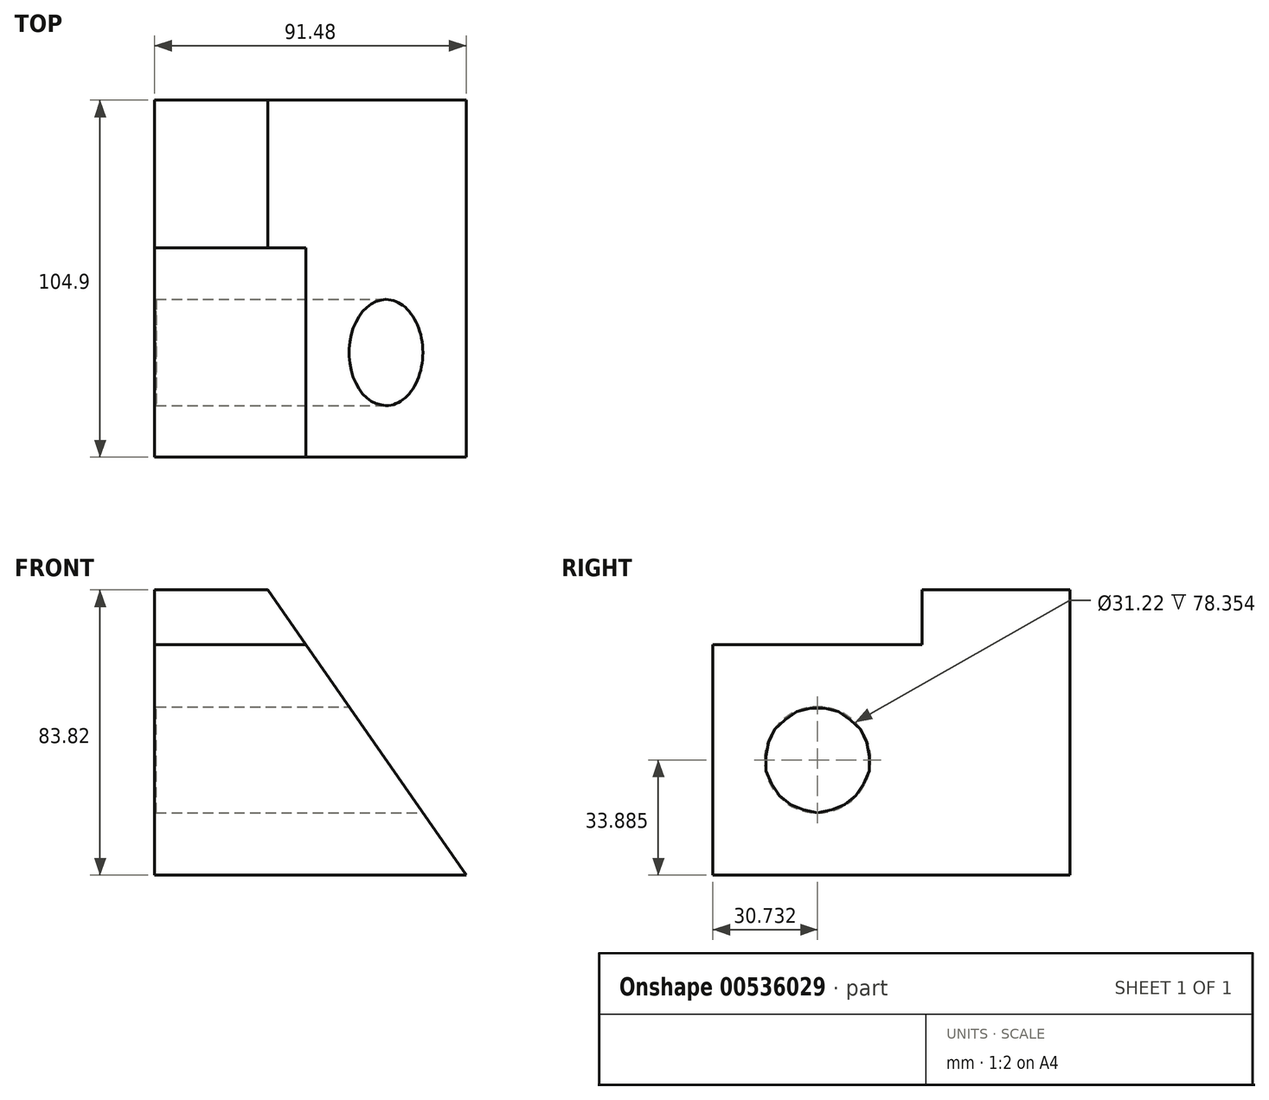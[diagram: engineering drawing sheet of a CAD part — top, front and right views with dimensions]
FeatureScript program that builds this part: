
annotation { "Feature Type Name" : "Feature", "Feature Type Description" : "" }
export const myFeature = defineFeature(function(context is Context, id is Id, definition is map)
    precondition{}
    {
        {
            var Q0;
            Q0=qCreatedBy(makeId("Front.planeOp"),FACE);
            var sketch = newSketch(context, id + "F0", { "sketchPlane" : qUnion([Q0])});
            skLineSegment(sketch, "E0.bottom", {"start": v(-57.07, 41.9) * mm, "end": v(57.07, 41.9) * mm});
            skLineSegment(sketch, "E0.top", {"start": v(-57.07, -41.9) * mm, "end": v(57.07, -41.9) * mm});
            skLineSegment(sketch, "E0.left", {"start": v(-57.07, 41.9) * mm, "end": v(-57.07, -41.9) * mm});
            skLineSegment(sketch, "E0.right", {"start": v(57.07, 41.9) * mm, "end": v(57.07, -41.9) * mm});
            skPoint(sketch, "E0.middle", {"position": v(0, 0) * mm});
            skLineSegment(sketch, "E1.bottom", {"start": v(-57.07, -41.9) * mm, "end": v(41.9, -41.9) * mm});
            skLineSegment(sketch, "E1.top", {"start": v(-57.07, 25.86) * mm, "end": v(41.9, 25.86) * mm});
            skLineSegment(sketch, "E1.left", {"start": v(-57.07, -41.9) * mm, "end": v(-57.07, 25.86) * mm});
            skLineSegment(sketch, "E1.right", {"start": v(41.9, -41.9) * mm, "end": v(41.9, 25.86) * mm});
            skSolve(sketch);
        }
        {
            var Q0;
            Q0 = qSketchRegion(id + "F0", true);
            extrude(context, id + "F1", {"entities" : qUnion([Q0]), "depth" : 25.4 * mm, "offsetDistance" : 25.4 * mm});
        }
        {
            var Q0;
            Q0=makeQuery(id+"F0.imprint","IMPRINT",FACE,{"disambiguationData":[TD([[makeQuery(id+"F0.imprint","IMPRINT",EDGE,{"derivedFrom":sQuery(id+"F0.wireOp",EDGE,"E0.bottom")}),-1.0]])]});
            extrude(context, id + "F2", {"entities" : qUnion([Q0]), "operationType" : NewBodyOperationType.ADD, "depth" : 43.43 * mm, "offsetDistance" : 25.4 * mm});
        }
        {
            var Q0;
            Q0=makeQuery(id+"F1.opExtrude","CAP_FACE",FACE,{"disambiguationData":[OSD([sQuery(id+"F0.wireOp",EDGE,"E0.bottom"),sQuery(id+"F0.wireOp",EDGE,"E0.top"),sQuery(id+"F0.wireOp",EDGE,"E0.left"),sQuery(id+"F0.wireOp",EDGE,"E0.right"),sQuery(id+"F0.wireOp",EDGE,"E1.bottom"),sQuery(id+"F0.wireOp",EDGE,"E1.left")])],"isStart":false});
            extrude(context, id + "F3", {"entities" : qUnion([Q0]), "operationType" : NewBodyOperationType.ADD, "depth" : 79.5 * mm, "offsetDistance" : 25.4 * mm});
        }
        {
            var Q0;
            Q0=makeQuery(id+"F3.opExtrude","SWEPT_FACE",FACE,{"disambiguationData":[OSD([sQuery(id+"F0.wireOp",EDGE,"E0.bottom"),sQuery(id+"F0.wireOp",EDGE,"E0.top"),sQuery(id+"F0.wireOp",EDGE,"E0.left"),sQuery(id+"F0.wireOp",EDGE,"E0.right"),sQuery(id+"F0.wireOp",EDGE,"E1.bottom"),sQuery(id+"F0.wireOp",EDGE,"E1.left"),sQuery(id+"F0.wireOp",EDGE,"E1.right")])]});
            var sketch = newSketch(context, id + "F4", { "sketchPlane" : qUnion([Q0])});
            skCircle(sketch, "E2", {"center": v(-74.17, -8.02) * mm, "radius": 15.61 * mm});
            skPoint(sketch, "E2.centerSnap0", {"position": v(-74.17, -41.9) * mm});
            skPoint(sketch, "E2.centerSnap1", {"position": v(-43.43, -8.02) * mm});
            skSolve(sketch);
        }
        {
            var Q0;
            Q0 = qSketchRegion(id + "F4", true);
            extrude(context, id + "F5", {"entities" : qUnion([Q0]), "operationType" : NewBodyOperationType.REMOVE, "oppositeDirection" : true, "depth" : 98.55 * mm, "offsetDistance" : 25.4 * mm});
        }
        {
            var Q0;
            Q0=makeQuery(id+"F3.opExtrude","CAP_FACE",FACE,{"disambiguationData":[OSD([sQuery(id+"F0.wireOp",EDGE,"E0.bottom"),sQuery(id+"F0.wireOp",EDGE,"E0.top"),sQuery(id+"F0.wireOp",EDGE,"E0.left"),sQuery(id+"F0.wireOp",EDGE,"E0.right"),sQuery(id+"F0.wireOp",EDGE,"E1.bottom"),sQuery(id+"F0.wireOp",EDGE,"E1.left")])],"isStart":false});
            var sketch = newSketch(context, id + "F6", { "sketchPlane" : qUnion([Q0])});
            skLineSegment(sketch, "E3", {"start": v(41.9, -41.9) * mm, "end": v(-7.58, 25.86) * mm});
            skSolve(sketch);
        }
        {
            var Q0;
            {var subQ0=sQuery(id+"F6.wireOp",EDGE,"E3");Q0=makeQuery(id+"F6.imprint","IMPRINT",FACE,{"disambiguationData":[TD([[makeQuery(id+"F6.imprint","IMPRINT",EDGE,{"derivedFrom":subQ0}),-1.0]])]});}
            extrude(context, id + "F7", {"entities" : qUnion([Q0]), "operationType" : NewBodyOperationType.REMOVE, "oppositeDirection" : true, "depth" : 61.47 * mm, "offsetDistance" : 25.4 * mm});
        }
        {
            var Q0;
            Q0=qCreatedBy(makeId("Front.planeOp"),FACE);
            var sketch = newSketch(context, id + "F8", { "sketchPlane" : qUnion([Q0])});
            skLineSegment(sketch, "E4", {"start": v(-28.92, 49.16) * mm, "end": v(43.7, -55.27) * mm});
            skLineSegment(sketch, "E5", {"start": v(43.7, -55.27) * mm, "end": v(114.33, -6.15) * mm});
            skLineSegment(sketch, "E6", {"start": v(114.33, -6.15) * mm, "end": v(40.17, 75.51) * mm});
            skLineSegment(sketch, "E7", {"start": v(40.17, 75.51) * mm, "end": v(-28.92, 49.16) * mm});
            skSolve(sketch);
        }
        {
            var Q0;
            Q0=makeQuery(id+"F8.imprint","IMPRINT",FACE,{"disambiguationData":[TD([[makeQuery(id+"F8.imprint","IMPRINT",EDGE,{"derivedFrom":sQuery(id+"F8.wireOp",EDGE,"E4")}),1.0]])]});
            extrude(context, id + "F9", {"entities" : qUnion([Q0]), "operationType" : NewBodyOperationType.REMOVE, "endBound" : BoundingType.SYMMETRIC, "oppositeDirection" : true, "depth" : 226.06 * mm, "offsetDistance" : 25.4 * mm});
        }
    });
